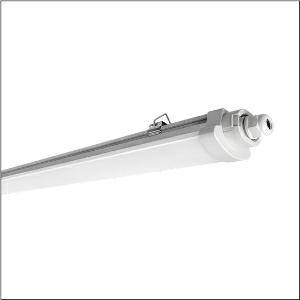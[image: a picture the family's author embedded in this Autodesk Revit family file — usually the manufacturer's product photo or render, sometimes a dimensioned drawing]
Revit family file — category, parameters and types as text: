
# Revit family: monsun_r__41_51fk20mk440a003_a901
name_source: partatom
category: Lighting Fixtures
units: mm (PartAtom-declared; Revit-internal decimal feet)

## family parameters
Cut with Voids When Loaded = No
Host = Face
Light Source = No
Part Type = Normal
Room Calculation Point = No
Round Connector Dimension = Use Diameter
Shared = No

## types (1)
- --- (1 x LED, 4000 lm, 30 W, 4000K)
    Apparent Load = 30 VA
    CIE Flux Codes = 44 74 92 92 100
    Color Rendering = 80
    Color Temperature = 4000K
    Default Elevation = 1800 mm
    Description = Monsun® 41, damp-proof luminaire, primary optical cover: diffuser, of PC, frosted, light emission: direct distribution, primary light characteristic: symmetric, installation type: surface-mounted, suspended mounting, LED, rated luminous flux: 4.000lm, luminous efficacy: 130lm/W, light colour: 840, colour temperature: 4000K, control gear: ECG Multilumen, with terminal, 3-pole, through-wiring: 3x 1.5mm², mains connection: 220..240V, AC, 50/60Hz, rated input power: 30W, housing, luminaire housing, of PC, grey, length: 1.200mm, width: 79mm, height: 52mm, end cap, of PC, grey, ceiling mounting element, of stainless steel (V2A), protection rating (complete): IP65, insulation class (complete): insulation class II (safety insulation), certification: CE, UKCA, protection symbol: D, impact resistance: IK08, permissible operating ambient temperature: -20..+35°C, corresponds to IFS (International Featured Standards) requirements for safety and quality in the food industry, contact your sales advisor before using the luminaires in applications with unclear chemical exposure, large temperature fluctuations or condensation-forming humidity, packaging unit: 1 piece
    Height = 54 mm
    Lamp = 1 x LED
    Lamp Light Flux = 4000 lm
    Lamp Power = 30 W
    Lamp count = 1
    Length = 1200 mm
    Luminous efficacy = 133 lm/W
    Manufacturer = Siteco
    ModVariant = No
    Model = 51FK20MK440A003
    Mounting Place = Ceiling
    Mounting Type = Surface mounted
    Number of Poles = 1
    OnlyDefault = Yes
    Power Factor = 1
    Product Name = Monsun® 41
    Product group = damp-proof luminaire
    ProductGroupID = 300
    Protection Class = Protection class II
    Protection Degree = IP 65
    RLX_Detail_Level = 1
    RLX_Emergency_Light_Flux = 0 lm
    RLX_Emergency_Type = 0
    RLX_Emergency_Type_DB = No
    RlxData = <blob elided: 31937 chars, md5=7c7c00ed>
    Socket = socket
    Standby Power = 0 W
    System Light Flux = 4000 lm
    System Power = 30 W
    Type Comments = factory setting: luminous flux: 100 % | (HIGH)
    Type Image = l_1007037.jpg
    URL = http://relux.com
    VarID = @adj_145807
    Voltage = 0 V
    Weight = 0.00 kg
    Width = 79 mm

## geometry (parser evidence)
native form markers: Blend x4, Sweep x14
no freeform markers — native parametric forms only
